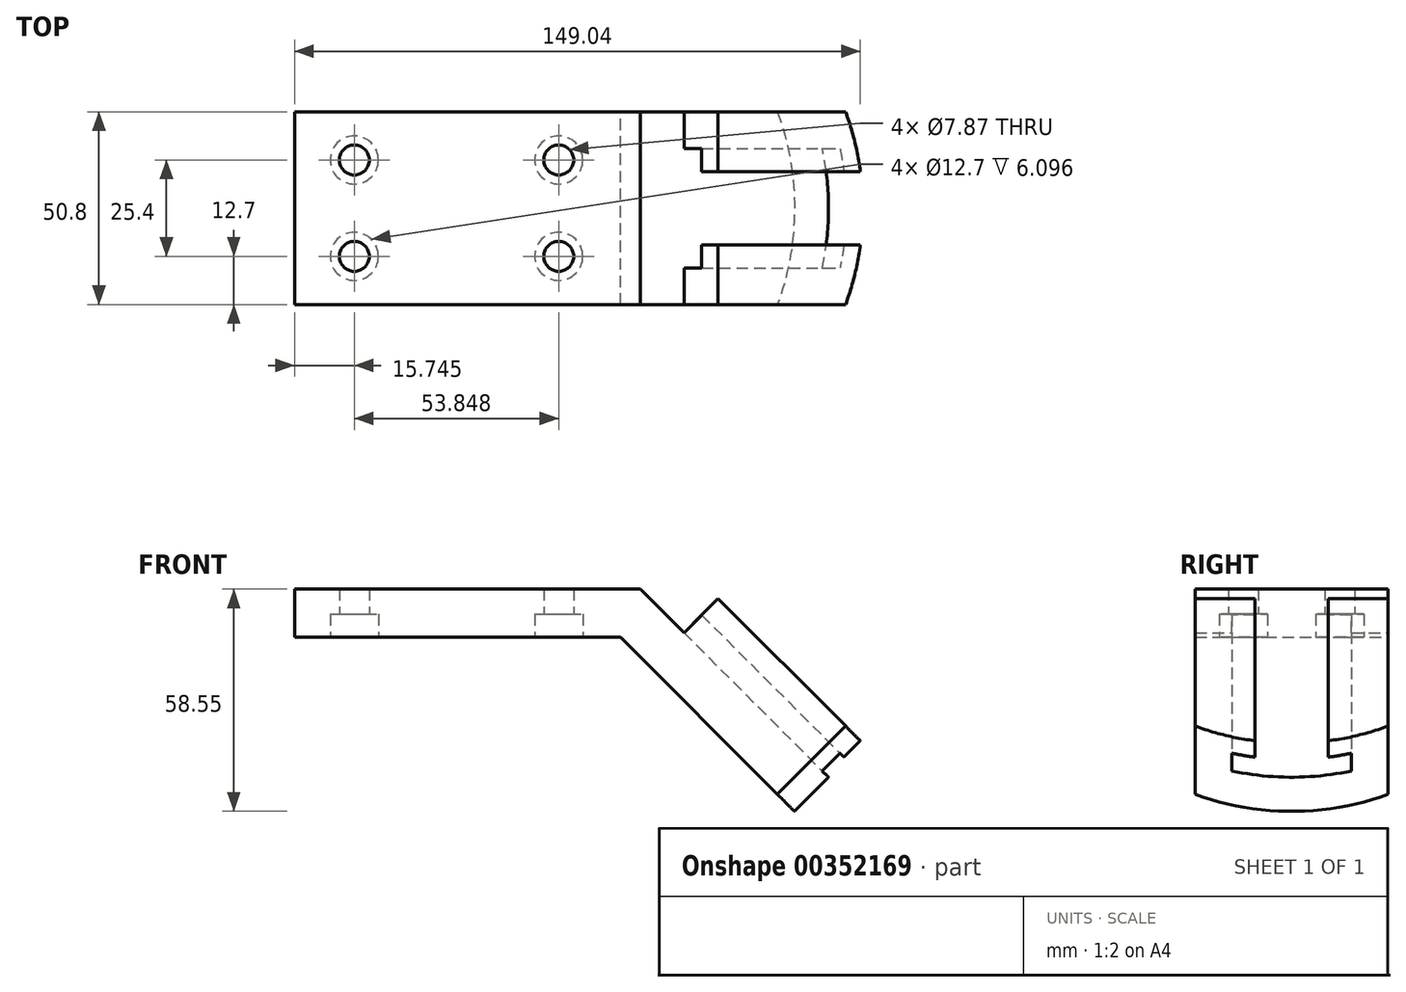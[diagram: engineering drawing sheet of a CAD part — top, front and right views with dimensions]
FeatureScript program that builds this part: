
annotation { "Feature Type Name" : "Feature", "Feature Type Description" : "" }
export const myFeature = defineFeature(function(context is Context, id is Id, definition is map)
    precondition{}
    {
        {
            var Q0;
            Q0=qCreatedBy(makeId("Front.planeOp"),FACE);
            var sketch = newSketch(context, id + "F0", { "sketchPlane" : qUnion([Q0])});
            skLineSegment(sketch, "E0.bottom", {"start": v(-91.11, 0) * mm, "end": v(-5.26, 0) * mm});
            skLineSegment(sketch, "E0.top", {"start": v(-91.11, 12.7) * mm, "end": v(0, 12.7) * mm});
            skLineSegment(sketch, "E0.left", {"start": v(-91.11, 0) * mm, "end": v(-91.11, 12.7) * mm});
            skLineSegment(sketch, "E1", {"start": v(0, 12.7) * mm, "end": v(11.5, 1.2) * mm});
            skLineSegment(sketch, "E2", {"start": v(49.57, -36.87) * mm, "end": v(40.6, -45.85) * mm});
            skLineSegment(sketch, "E3", {"start": v(40.6, -45.85) * mm, "end": v(-5.26, 0) * mm});
            skLineSegment(sketch, "E4", {"start": v(11.5, 1.2) * mm, "end": v(20.47, 10.19) * mm});
            skLineSegment(sketch, "E5", {"start": v(20.47, 10.19) * mm, "end": v(58.55, -27.9) * mm});
            skLineSegment(sketch, "E6", {"start": v(58.55, -27.9) * mm, "end": v(49.57, -36.87) * mm});
            skSolve(sketch);
        }
        {
            var Q0;
            Q0 = qSketchRegion(id + "F0", true);
            extrude(context, id + "F1", {"entities" : qUnion([Q0]), "endBound" : BoundingType.SYMMETRIC, "depth" : 50.8 * mm});
        }
        {
            var Q0;
            Q0=makeQuery(id+"F1.opExtrude","SWEPT_FACE",FACE,{"disambiguationData":[OSD([sQuery(id+"F0.wireOp",EDGE,"E0.bottom")])]});
            var sketch = newSketch(context, id + "F2", { "sketchPlane" : qUnion([Q0])});
            skLineSegment(sketch, "E7.direction1", {"start": v(-75.36, -12.7) * mm, "end": v(-21.52, -12.7) * mm, "construction": true});
            skLineSegment(sketch, "E7.direction2", {"start": v(-75.36, -12.7) * mm, "end": v(-75.36, 12.7) * mm, "construction": true});
            skPoint(sketch, "E8", {"position": v(-21.52, 12.7) * mm});
            skSolve(sketch);
        }
        {
            var Q0;
            Q0=sQuery(id+"F2.wireOp",VERTEX,"E7.direction2.end");
            var Q1;
            Q1=sQuery(id+"F2.wireOp",VERTEX,"E7.direction2.start");
            var Q2;
            Q2=sQuery(id+"F2.wireOp",VERTEX,"E7.direction1.end");
            var Q3;
            Q3=sQuery(id+"F2.wireOp",VERTEX,"E8");
            var Q4;
            Q4=makeQuery(id+"F1.opExtrude","SWEPT_BODY",BODY,{"disambiguationData":[OSD([sQuery(id+"F0.wireOp",EDGE,"E0.bottom"),sQuery(id+"F0.wireOp",EDGE,"E0.top"),sQuery(id+"F0.wireOp",EDGE,"E0.left"),sQuery(id+"F0.wireOp",EDGE,"E1"),sQuery(id+"F0.wireOp",EDGE,"E2"),sQuery(id+"F0.wireOp",EDGE,"E3"),sQuery(id+"F0.wireOp",EDGE,"E4"),sQuery(id+"F0.wireOp",EDGE,"E5"),sQuery(id+"F0.wireOp",EDGE,"E6")])]});
            hole(context, id + "F3", {"style" : HoleStyle.C_BORE, "endStyle" : HoleEndStyle.THROUGH, "holeDiameter" : 7.87 * mm, "cBoreDiameter" : 12.7 * mm, "cBoreDepth" : 6.1 * mm, "isTappedThrough" : true, "tappedDepth" : 12.7 * mm, "tapClearance" : 3, "locations" : qUnion([Q0, Q1, Q2, Q3]), "scope" : qUnion([Q4])});
        }
        {
            var Q0;
            Q0=makeQuery(id+"F1.opExtrude","SWEPT_FACE",FACE,{"disambiguationData":[OSD([sQuery(id+"F0.wireOp",EDGE,"E2"),sQuery(id+"F0.wireOp",EDGE,"E6")])]});
            var sketch = newSketch(context, id + "F4", { "sketchPlane" : qUnion([Q0])});
            skLineSegment(sketch, "E9.bottom", {"start": v(-9.65, 21.68) * mm, "end": v(9.65, 21.68) * mm});
            skLineSegment(sketch, "E9.left", {"start": v(-9.65, 21.68) * mm, "end": v(-9.65, 15.58) * mm});
            skLineSegment(sketch, "E9.right", {"start": v(9.65, 21.68) * mm, "end": v(9.65, 15.58) * mm});
            skLineSegment(sketch, "E10.bottom", {"start": v(-15.75, 15.58) * mm, "end": v(-9.65, 15.58) * mm});
            skLineSegment(sketch, "E10.top", {"start": v(-15.75, 8.98) * mm, "end": v(15.75, 8.98) * mm});
            skLineSegment(sketch, "E10.left", {"start": v(-15.75, 15.58) * mm, "end": v(-15.75, 8.98) * mm});
            skLineSegment(sketch, "E10.right", {"start": v(15.75, 15.58) * mm, "end": v(15.75, 8.98) * mm});
            skPoint(sketch, "E11", {"position": v(0, 21.68) * mm});
            skPoint(sketch, "E12", {"position": v(0, 8.98) * mm});
            skLineSegment(sketch, "E13.trimOffspring", {"start": v(9.65, 15.58) * mm, "end": v(15.75, 15.58) * mm});
            skSolve(sketch);
        }
        {
            var Q0;
            Q0 = qSketchRegion(id + "F4", true);
            extrude(context, id + "F5", {"entities" : qUnion([Q0]), "operationType" : NewBodyOperationType.REMOVE, "endBound" : BoundingType.THROUGH_ALL, "oppositeDirection" : true, "depth" : 25.4 * mm});
        }
        {
            var Q0;
            {var subQ1=sQuery(id+"F0.wireOp",EDGE,"E5");Q0=makeQuery(id+"F5.boolean.opBoolean","SPLIT",FACE,{"disambiguationData":[TD([makeQuery(id+"F5.opExtrude","SWEPT_FACE",FACE,{"disambiguationData":[OSD([sQuery(id+"F4.wireOp",EDGE,"E9.right")])]})])],"derivedFrom":makeQuery(id+"F1.opExtrude","SWEPT_FACE",FACE,{"disambiguationData":[OSD([subQ1])]})});}
            var sketch = newSketch(context, id + "F6", { "sketchPlane" : qUnion([Q0])});
            skArc(sketch, "E14", {"start": v(53.85, -7.28) * mm, "mid": v(0, -61.12) * mm, "end": v(-53.85, -7.28) * mm});
            skLineSegment(sketch, "E15", {"start": v(53.85, -7.28) * mm, "end": v(-53.85, -7.28) * mm});
            skLineSegment(sketch, "E16", {"start": v(53.85, -7.28) * mm, "end": v(31.52, 119.55) * mm});
            skLineSegment(sketch, "E17", {"start": v(31.52, 119.55) * mm, "end": v(-64.2, 119.55) * mm});
            skLineSegment(sketch, "E18", {"start": v(-64.2, 119.55) * mm, "end": v(-53.85, -7.28) * mm});
            skSolve(sketch);
        }
        {
            var Q0;
            Q0 = qSketchRegion(id + "F6", true);
            extrude(context, id + "F7", {"entities" : qUnion([Q0]), "operationType" : NewBodyOperationType.INTERSECT, "endBound" : BoundingType.THROUGH_ALL, "oppositeDirection" : true, "depth" : 25.4 * mm});
        }
    });
